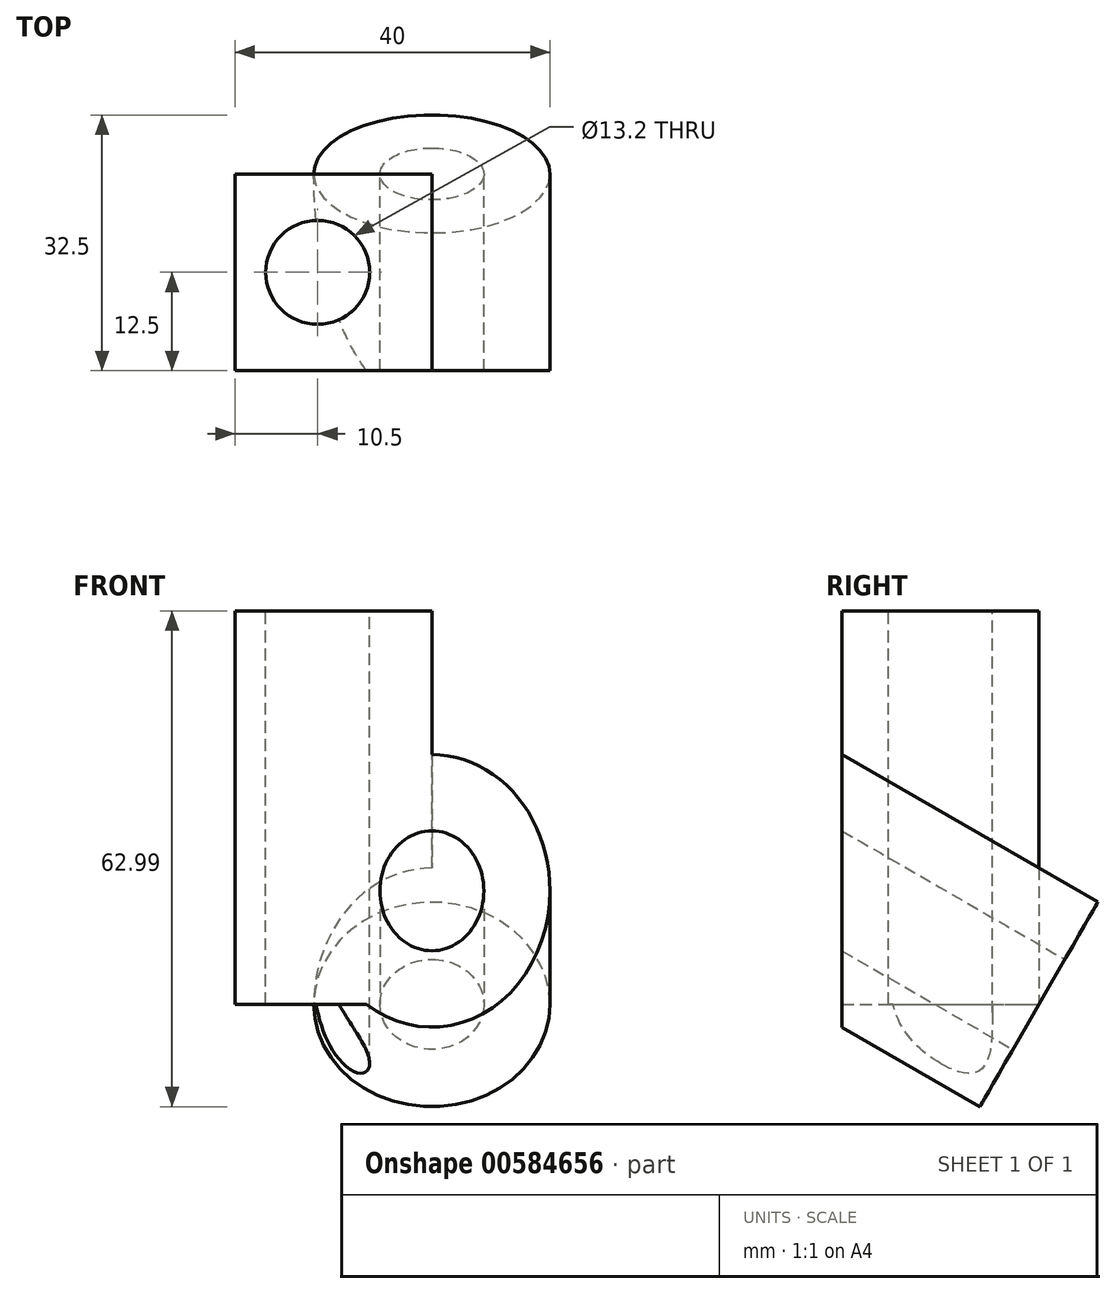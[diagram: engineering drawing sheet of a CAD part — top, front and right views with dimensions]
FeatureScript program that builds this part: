
annotation { "Feature Type Name" : "Feature", "Feature Type Description" : "" }
export const myFeature = defineFeature(function(context is Context, id is Id, definition is map)
    precondition{}
    {
        {
            var Q0;
            Q0=qCreatedBy(makeId("Front.planeOp"),FACE);
            var sketch = newSketch(context, id + "F0", { "sketchPlane" : qUnion([Q0])});
            skLineSegment(sketch, "E0.bottom", {"start": v(17.5, -25) * mm, "end": v(-17.5, -25) * mm});
            skLineSegment(sketch, "E0.top", {"start": v(17.5, 25) * mm, "end": v(-17.5, 25) * mm});
            skLineSegment(sketch, "E0.left", {"start": v(17.5, -25) * mm, "end": v(17.5, 25) * mm});
            skLineSegment(sketch, "E0.right", {"start": v(-17.5, -25) * mm, "end": v(-17.5, 25) * mm});
            skPoint(sketch, "E0.middle", {"position": v(0, 0) * mm});
            skSolve(sketch);
        }
        {
            var Q0;
            Q0=qSketchRegion(id+"F0",true);
            extrude(context, id + "F1", {"entities" : qUnion([Q0]), "depth" : 25 * mm, "offsetDistance" : 25 * mm});
        }
        {
            var Q0;
            Q0=makeQuery(id+"F1.opExtrude","CAP_FACE",FACE,{"disambiguationData":[OSD([sQuery(id+"F0.wireOp",EDGE,"E0.bottom"),sQuery(id+"F0.wireOp",EDGE,"E0.top"),sQuery(id+"F0.wireOp",EDGE,"E0.left"),sQuery(id+"F0.wireOp",EDGE,"E0.right"),sQuery(id+"F0.wireOp",EDGE,"3PXkUS2k-hGXQ-lu6G-6GVv-WeRPOjVUKZ5q")])],"isStart":true});
            var Q1;
            Q1=makeQuery(id+"F1.opExtrude","CAP_EDGE",EDGE,{"disambiguationData":[OSD([sQuery(id+"F0.wireOp",EDGE,"E0.bottom")])],"isStart":true});
            cPlane(context, id + "F2", {"entities" : qUnion([Q0, Q1]), "cplaneType" : CPlaneType.LINE_ANGLE, "offset" : 25 * mm, "angle" : 30 * degree, "width" : 150 * mm, "height" : 150 * mm});
        }
        {
            var Q0;
            Q0=qCreatedBy(id+"F2.planeOp",FACE);
            var sketch = newSketch(context, id + "F3", { "sketchPlane" : qUnion([Q0])});
            skCircle(sketch, "E1", {"center": v(17.5, -21.65) * mm, "radius": 15 * mm});
            skSolve(sketch);
        }
        {
            var Q0;
            Q0=qSketchRegion(id+"F3",true);
            extrude(context, id + "F4", {"entities" : qUnion([Q0]), "operationType" : NewBodyOperationType.ADD, "depth" : 52 * mm, "offsetDistance" : 25 * mm});
        }
        {
            var Q0;
            Q0=makeQuery(id+"F4.opExtrude","CAP_FACE",FACE,{"disambiguationData":[OSD([sQuery(id+"F3.wireOp",EDGE,"E1")])],"isStart":true});
            var sketch = newSketch(context, id + "F5", { "sketchPlane" : qUnion([Q0])});
            skPoint(sketch, "E2", {"position": v(-17.5, -21.65) * mm});
            skSolve(sketch);
        }
        {
            var Q0;
            Q0=sQuery(id+"F5.wireOp",VERTEX,"E2");
            var Q1;
            Q1=makeQuery(id+"F1.opExtrude","SWEPT_BODY",BODY,{"disambiguationData":[OSD([sQuery(id+"F0.wireOp",EDGE,"E0.bottom"),sQuery(id+"F0.wireOp",EDGE,"E0.top"),sQuery(id+"F0.wireOp",EDGE,"E0.left"),sQuery(id+"F0.wireOp",EDGE,"E0.right"),sQuery(id+"F0.wireOp",EDGE,"3PXkUS2k-hGXQ-lu6G-6GVv-WeRPOjVUKZ5q")])]});
            hole(context, id + "F6", {"style" : HoleStyle.C_BORE, "endStyle" : HoleEndStyle.THROUGH, "holeDiameter" : 13.2 * mm, "cBoreDiameter" : 19.25 * mm, "cBoreDepth" : 0 * mm, "majorDiameter" : 5 * mm, "isTappedThrough" : true, "tappedDepth" : 12 * mm, "tapClearance" : 3, "startFromSketch" : true, "locations" : qUnion([Q0]), "scope" : qUnion([Q1])});
        }
        {
            var Q0;
            Q0=makeQuery(id+"F1.opExtrude","SWEPT_FACE",FACE,{"disambiguationData":[OSD([sQuery(id+"F0.wireOp",EDGE,"E0.top")])]});
            var sketch = newSketch(context, id + "F7", { "sketchPlane" : qUnion([Q0])});
            skPoint(sketch, "E3", {"position": v(3, -12.5) * mm});
            skPoint(sketch, "E3.positionSnap0", {"position": v(17.5, -12.5) * mm});
            skSolve(sketch);
        }
        {
            var Q0;
            Q0=sQuery(id+"F7.wireOp",VERTEX,"E3");
            var Q1;
            Q1=makeQuery(id+"F1.opExtrude","SWEPT_BODY",BODY,{"disambiguationData":[OSD([sQuery(id+"F0.wireOp",EDGE,"E0.bottom"),sQuery(id+"F0.wireOp",EDGE,"E0.top"),sQuery(id+"F0.wireOp",EDGE,"E0.left"),sQuery(id+"F0.wireOp",EDGE,"E0.right")])]});
            hole(context, id + "F8", {"style" : HoleStyle.C_BORE, "endStyle" : HoleEndStyle.THROUGH, "holeDiameter" : 13.2 * mm, "cBoreDiameter" : 19.25 * mm, "cBoreDepth" : 0 * mm, "majorDiameter" : 5 * mm, "isTappedThrough" : true, "tappedDepth" : 12 * mm, "tapClearance" : 3, "startFromSketch" : true, "locations" : qUnion([Q0]), "scope" : qUnion([Q1])});
        }
        {
            var Q0;
            Q0=makeQuery(id+"F1.opExtrude","SWEPT_FACE",FACE,{"disambiguationData":[OSD([sQuery(id+"F0.wireOp",EDGE,"E0.right")])]});
            var sketch = newSketch(context, id + "F9", { "sketchPlane" : qUnion([Q0])});
            skLineSegment(sketch, "E4.bottom", {"start": v(25, -29.5) * mm, "end": v(54.24, -29.5) * mm});
            skLineSegment(sketch, "E4.top", {"start": v(25, 26.98) * mm, "end": v(54.24, 26.98) * mm});
            skLineSegment(sketch, "E4.left", {"start": v(25, -29.5) * mm, "end": v(25, 26.98) * mm});
            skLineSegment(sketch, "E4.right", {"start": v(54.24, -29.5) * mm, "end": v(54.24, 26.98) * mm});
            skSolve(sketch);
        }
        {
            var Q0;
            Q0 = qSketchRegion(id + "F9", true);
            extrude(context, id + "F10", {"entities" : qUnion([Q0]), "operationType" : NewBodyOperationType.REMOVE, "oppositeDirection" : true, "depth" : 60 * mm, "offsetDistance" : 25 * mm});
        }
        {
            var Q0;
            Q0=makeQuery(id+"F1.opExtrude","CAP_FACE",FACE,{"disambiguationData":[OSD([sQuery(id+"F0.wireOp",EDGE,"E0.bottom"),sQuery(id+"F0.wireOp",EDGE,"E0.top"),sQuery(id+"F0.wireOp",EDGE,"E0.left"),sQuery(id+"F0.wireOp",EDGE,"E0.right")])],"isStart":true});
            var sketch = newSketch(context, id + "F11", { "sketchPlane" : qUnion([Q0])});
            skLineSegment(sketch, "E5.bottom", {"start": v(17.5, 25) * mm, "end": v(7.5, 25) * mm});
            skLineSegment(sketch, "E5.top", {"start": v(17.5, -25) * mm, "end": v(7.5, -25) * mm});
            skLineSegment(sketch, "E5.left", {"start": v(17.5, 25) * mm, "end": v(17.5, -25) * mm});
            skLineSegment(sketch, "E5.right", {"start": v(7.5, 25) * mm, "end": v(7.5, -25) * mm});
            skSolve(sketch);
        }
        {
            var Q0;
            Q0 = qSketchRegion(id + "F11", true);
            extrude(context, id + "F12", {"entities" : qUnion([Q0]), "operationType" : NewBodyOperationType.REMOVE, "oppositeDirection" : true, "depth" : 25 * mm, "offsetDistance" : 25 * mm});
        }
    });
